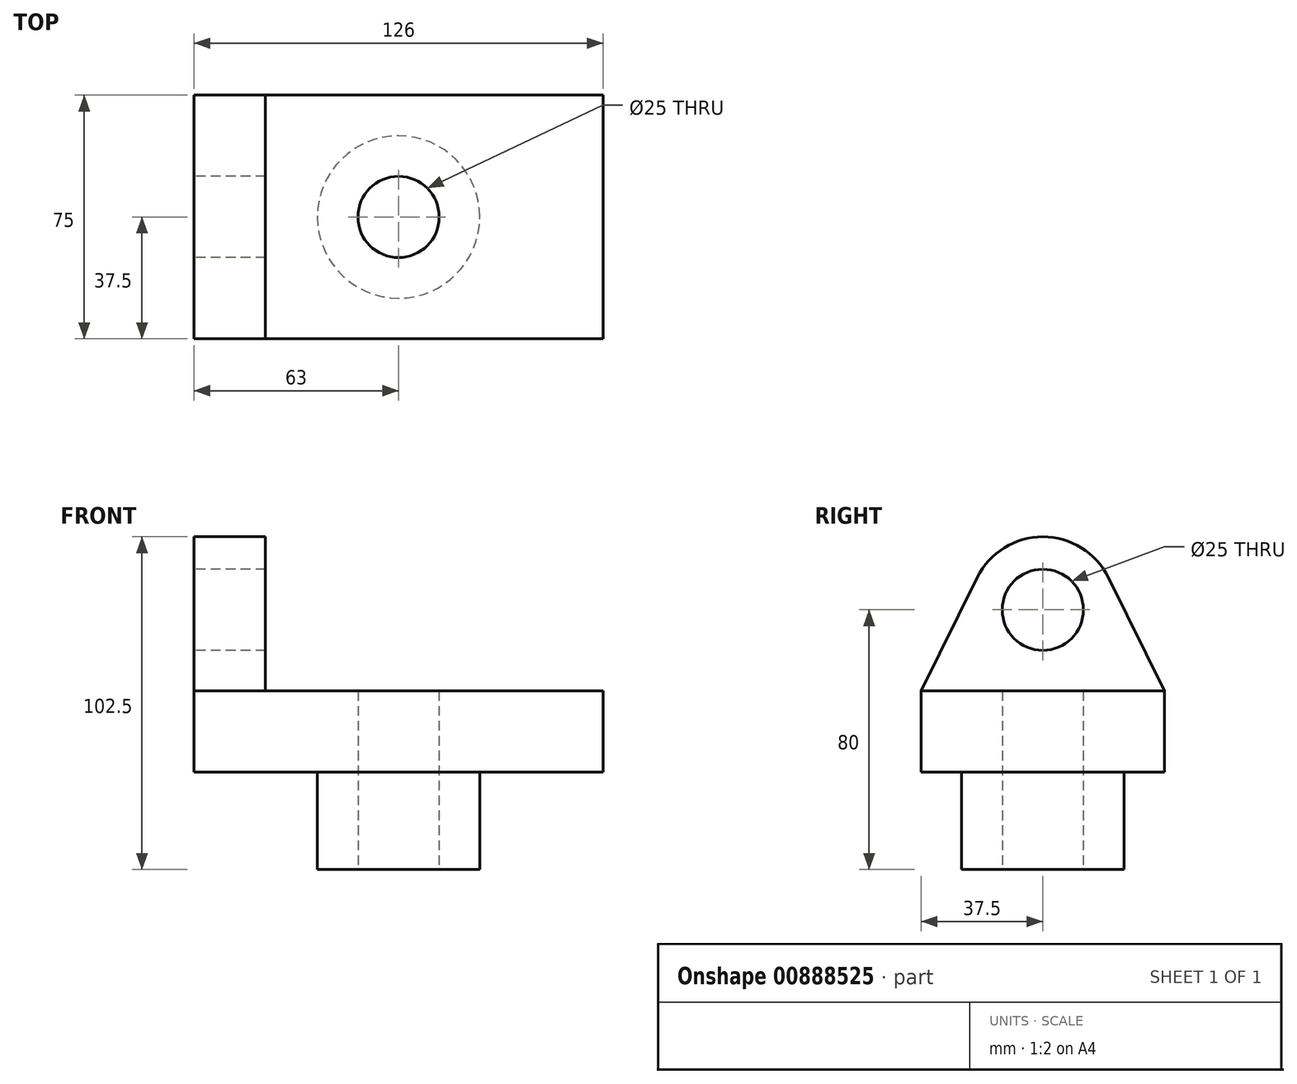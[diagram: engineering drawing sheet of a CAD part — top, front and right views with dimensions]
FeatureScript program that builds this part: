
annotation { "Feature Type Name" : "Feature", "Feature Type Description" : "" }
export const myFeature = defineFeature(function(context is Context, id is Id, definition is map)
    precondition{}
    {
        {
            var Q0;
            Q0=qCreatedBy(makeId("Front.planeOp"),FACE);
            var sketch = newSketch(context, id + "F0", { "sketchPlane" : qUnion([Q0])});
            skLineSegment(sketch, "E0.bottom", {"start": v(37.5, -12.5) * mm, "end": v(-37.5, -12.5) * mm});
            skLineSegment(sketch, "E0.top", {"start": v(37.5, 12.5) * mm, "end": v(-37.5, 12.5) * mm});
            skLineSegment(sketch, "E0.left", {"start": v(37.5, -12.5) * mm, "end": v(37.5, 12.5) * mm});
            skLineSegment(sketch, "E0.right", {"start": v(-37.5, -12.5) * mm, "end": v(-37.5, 12.5) * mm});
            skPoint(sketch, "E0.middle", {"position": v(0, 0) * mm});
            skSolve(sketch);
        }
        {
            var Q0;
            Q0=makeQuery(id+"F0.imprint","IMPRINT",FACE,{"disambiguationData":[TD([[makeQuery(id+"F0.imprint","IMPRINT",EDGE,{"derivedFrom":sQuery(id+"F0.wireOp",EDGE,"E0.bottom")}),-1.0]])]});
            extrude(context, id + "F1", {"entities" : qUnion([Q0]), "depth" : (82 + 44) * mm, "offsetDistance" : 25 * mm, "symmetric" : true});
        }
        {
            var Q0;
            Q0=makeQuery(id+"F1.opExtrude","CAP_FACE",FACE,{"disambiguationData":[OSD([sQuery(id+"F0.wireOp",EDGE,"E0.bottom"),sQuery(id+"F0.wireOp",EDGE,"E0.top"),sQuery(id+"F0.wireOp",EDGE,"E0.left"),sQuery(id+"F0.wireOp",EDGE,"E0.right")])],"isStart":false});
            var sketch = newSketch(context, id + "F2", { "sketchPlane" : qUnion([Q0])});
            skLineSegment(sketch, "E1", {"start": v(19.7, 37.5) * mm, "end": v(-22.5, 37.5) * mm, "construction": true});
            skCircle(sketch, "E2", {"center": v(0, 37.5) * mm, "radius": 12.5 * mm});
            skArc(sketch, "E3", {"start": v(20.16, 47.5) * mm, "mid": v(0, 60) * mm, "end": v(-20.16, 47.5) * mm});
            skLineSegment(sketch, "E4", {"start": v(37.5, 12.5) * mm, "end": v(20.16, 47.5) * mm});
            skLineSegment(sketch, "E5.MirrorCS", {"start": v(-37.5, 12.5) * mm, "end": v(-20.16, 47.5) * mm});
            skLineSegment(sketch, "E6.trimOffspring", {"start": v(-25.11, 37.5) * mm, "end": v(-35.99, 37.5) * mm, "construction": true});
            skSolve(sketch);
        }
        {
            var Q0;
            Q0=makeQuery(id+"F2.imprint","IMPRINT",FACE,{"disambiguationData":[TD([[makeQuery(id+"F2.imprint","IMPRINT",EDGE,{"derivedFrom":sQuery(id+"F2.wireOp",EDGE,"E2")}),-1.0]])]});
            extrude(context, id + "F3", {"entities" : qUnion([Q0]), "operationType" : NewBodyOperationType.ADD, "oppositeDirection" : true, "depth" : 22 * mm, "offsetDistance" : 25 * mm});
        }
        {
            var Q0;
            Q0=qCreatedBy(makeId("Right.planeOp"),FACE);
            var sketch = newSketch(context, id + "F4", { "sketchPlane" : qUnion([Q0])});
            skLineSegment(sketch, "E7", {"start": v(0, 73.43) * mm, "end": v(0, -33.12) * mm, "construction": true});
            skSolve(sketch);
        }
        {
            var Q0;
            Q0=makeQuery(id+"F1.opExtrude","SWEPT_BODY",BODY,{"disambiguationData":[OSD([sQuery(id+"F0.wireOp",EDGE,"E0.bottom"),sQuery(id+"F0.wireOp",EDGE,"E0.top"),sQuery(id+"F0.wireOp",EDGE,"E0.left"),sQuery(id+"F0.wireOp",EDGE,"E0.right")])]});
            var Q1;
            Q1=sQuery(id+"F4.wireOp",EDGE,"E7");
            transform(context, id + "F5", {"entities" : qUnion([Q0]), "transformType" : TransformType.ROTATION, "transformAxis" : qUnion([Q1]), "angle" : 90 * degree, "makeCopy" : false});
        }
        {
            var Q0;
            Q0=makeQuery(id+"F1.opExtrude","SWEPT_FACE",FACE,{"disambiguationData":[OSD([sQuery(id+"F0.wireOp",EDGE,"E0.bottom")])]});
            var sketch = newSketch(context, id + "F6", { "sketchPlane" : qUnion([Q0])});
            skCircle(sketch, "E8", {"center": v(0, 0) * mm, "radius": 25 * mm});
            skSolve(sketch);
        }
        {
            var Q0;
            Q0=makeQuery(id+"F6.imprint","IMPRINT",FACE,{"disambiguationData":[TD([[makeQuery(id+"F6.imprint","IMPRINT",EDGE,{"derivedFrom":sQuery(id+"F6.wireOp",EDGE,"E8")}),1.0]])]});
            extrude(context, id + "F7", {"entities" : qUnion([Q0]), "operationType" : NewBodyOperationType.ADD, "depth" : 30 * mm, "offsetDistance" : 25 * mm});
        }
        {
            var Q0;
            Q0=makeQuery(id+"F7.opExtrude","CAP_FACE",FACE,{"disambiguationData":[OSD([sQuery(id+"F6.wireOp",EDGE,"E8")])],"isStart":false});
            var sketch = newSketch(context, id + "F8", { "sketchPlane" : qUnion([Q0])});
            skCircle(sketch, "E9", {"center": v(0, 0) * mm, "radius": 12.5 * mm});
            skSolve(sketch);
        }
        {
            var Q0;
            Q0=makeQuery(id+"F8.imprint","IMPRINT",FACE,{"disambiguationData":[TD([[makeQuery(id+"F8.imprint","IMPRINT",EDGE,{"derivedFrom":sQuery(id+"F8.wireOp",EDGE,"E9")}),1.0]])]});
            extrude(context, id + "F9", {"entities" : qUnion([Q0]), "operationType" : NewBodyOperationType.REMOVE, "endBound" : BoundingType.THROUGH_ALL, "oppositeDirection" : true, "depth" : 25 * mm, "offsetDistance" : 25 * mm});
        }
    });
